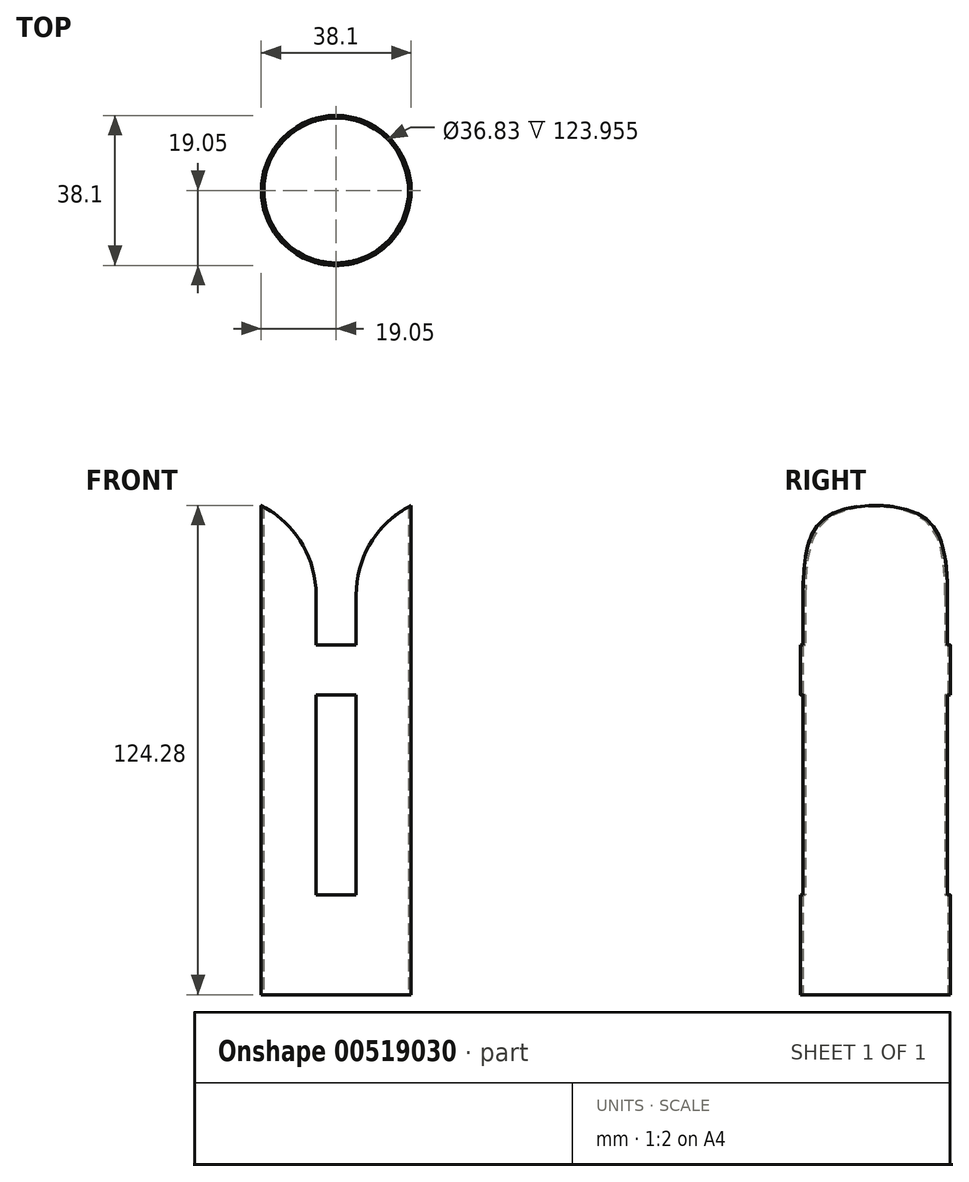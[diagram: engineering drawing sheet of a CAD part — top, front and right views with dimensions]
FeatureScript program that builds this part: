
annotation { "Feature Type Name" : "Feature", "Feature Type Description" : "" }
export const myFeature = defineFeature(function(context is Context, id is Id, definition is map)
    precondition{}
    {
        {
            var Q0;
            Q0=qCreatedBy(makeId("Top.planeOp"),FACE);
            var sketch = newSketch(context, id + "F0", { "sketchPlane" : qUnion([Q0])});
            skCircle(sketch, "E0", {"center": v(0, 0) * mm, "radius": 19.05 * mm});
            skSolve(sketch);
        }
        {
            var Q0;
            Q0=makeQuery(id+"F0.imprint","IMPRINT",FACE,{"disambiguationData":[TD([[makeQuery(id+"F0.imprint","IMPRINT",EDGE,{"derivedFrom":sQuery(id+"F0.wireOp",EDGE,"E0")}),1.0]])]});
            extrude(context, id + "F1", {"entities" : qUnion([Q0]), "depth" : 127 * mm, "offsetDistance" : 25.4 * mm});
        }
        {
            var Q0;
            Q0=makeQuery(id+"F1.opExtrude","CAP_FACE",FACE,{"disambiguationData":[OSD([sQuery(id+"F0.wireOp",EDGE,"E0")])],"isStart":true});
            var Q1;
            Q1=makeQuery(id+"F1.opExtrude","CAP_FACE",FACE,{"disambiguationData":[OSD([sQuery(id+"F0.wireOp",EDGE,"E0")])],"isStart":false});
            shell(context, id + "F2", {"entities" : qUnion([Q0, Q1]), "thickness" : 0.64 * mm});
        }
        {
            var Q0;
            Q0=qCreatedBy(makeId("Front.planeOp"),FACE);
            var sketch = newSketch(context, id + "F3", { "sketchPlane" : qUnion([Q0])});
            skLineSegment(sketch, "E1.bottom", {"start": v(5.08, 76.2) * mm, "end": v(-5.08, 76.2) * mm});
            skLineSegment(sketch, "E1.top", {"start": v(5.08, 25.4) * mm, "end": v(-5.08, 25.4) * mm});
            skLineSegment(sketch, "E1.left", {"start": v(5.08, 76.2) * mm, "end": v(5.08, 25.4) * mm});
            skLineSegment(sketch, "E1.right", {"start": v(-5.08, 76.2) * mm, "end": v(-5.08, 25.4) * mm});
            skPoint(sketch, "E1.middle", {"position": v(0, 50.8) * mm});
            skLineSegment(sketch, "E2.bottom", {"start": v(5.08, 139.7) * mm, "end": v(-5.08, 139.7) * mm});
            skLineSegment(sketch, "E2.top", {"start": v(5.08, 88.9) * mm, "end": v(-5.08, 88.9) * mm});
            skLineSegment(sketch, "E2.left", {"start": v(5.08, 139.7) * mm, "end": v(5.08, 88.9) * mm});
            skLineSegment(sketch, "E2.right", {"start": v(-5.08, 139.7) * mm, "end": v(-5.08, 88.9) * mm});
            skPoint(sketch, "E2.middle", {"position": v(0, 114.3) * mm});
            skLineSegment(sketch, "E3.bottom", {"start": v(4.64, 276.86) * mm, "end": v(-5.52, 276.86) * mm});
            skLineSegment(sketch, "E3.top", {"start": v(4.64, 149.86) * mm, "end": v(-5.52, 149.86) * mm});
            skLineSegment(sketch, "E3.left", {"start": v(4.64, 276.86) * mm, "end": v(4.64, 149.86) * mm});
            skLineSegment(sketch, "E3.right", {"start": v(-5.52, 276.86) * mm, "end": v(-5.52, 149.86) * mm});
            skPoint(sketch, "E3.middle", {"position": v(-0.44, 213.36) * mm});
            skSolve(sketch);
        }
        {
            var Q0;
            Q0=qSketchRegion(id+"F3",true);
            extrude(context, id + "F4", {"entities" : qUnion([Q0]), "operationType" : NewBodyOperationType.REMOVE, "endBound" : BoundingType.SYMMETRIC, "depth" : 76.2 * mm});
        }
        {
            var Q0;
            Q0=makeQuery(id+"F4.boolean.opBoolean","INTERSECT",EDGE,{"disambiguationData":[OD(0.0)],"derivedFrom":[makeQuery(id+"F1.opExtrude","CAP_FACE",FACE,{"disambiguationData":[OSD([sQuery(id+"F0.wireOp",EDGE,"E0")])],"isStart":false}),makeQuery(id+"F4.opExtrude","SWEPT_FACE",FACE,{"disambiguationData":[OSD([sQuery(id+"F3.wireOp",EDGE,"E2.right")])]})]});
            var Q1;
            Q1=makeQuery(id+"F4.boolean.opBoolean","INTERSECT",EDGE,{"disambiguationData":[OD(0.0)],"derivedFrom":[makeQuery(id+"F1.opExtrude","CAP_FACE",FACE,{"disambiguationData":[OSD([sQuery(id+"F0.wireOp",EDGE,"E0")])],"isStart":false}),makeQuery(id+"F4.opExtrude","SWEPT_FACE",FACE,{"disambiguationData":[OSD([sQuery(id+"F3.wireOp",EDGE,"E2.left")])]})]});
            fillet(context, id + "F5", {"entities" : qUnion([Q0, Q1]), "radius" : 25.4 * mm, "allowEdgeOverflow" : false});
        }
    });
